# Revit family: SS-1
name_source: partatom
category: Plumbing Fixtures
revit_build: Autodesk Revit 2014 (Build: 20130308_1515(x64)
units: mm (PartAtom-declared; Revit-internal decimal feet)

## types (1)
- SS-1
    Certification = http://www.helvex.com.mx
    Description = Hardness Water Softener or Conditioner
    Documentation = http://www.helvex.com.mx
    Features = Protects Against Damage Of Sales Scale, Oxide And Corrosion, Cost Savings Through Better Use Of Energy In The Area Of Hot Water, Extended Duration Of Life Commercial Machinery And Equipment, Saving Time And Clean Costs Less, Cost Less Maintenance Of Feed-Water Heater And Distributing Reservoir
    Instructive = http://www.helvex.com.mx
    Manufacturer = HELVEX
    Maximum Tubular = Ø 25,4 mm (Ø1")
    Model = SS-1
    Power Consumption = 5 W
    Transformer Sealing Voltage = Input: 110-240 Vca 50/60 Hz, 0.5 A; Output: 18.8 Vca, 13.5 VA
    Type Comments = Special Products
    URL = http://www.helvex.com.mx

## geometry (parser evidence)
native form markers: Sweep x3
no freeform markers — native parametric forms only
